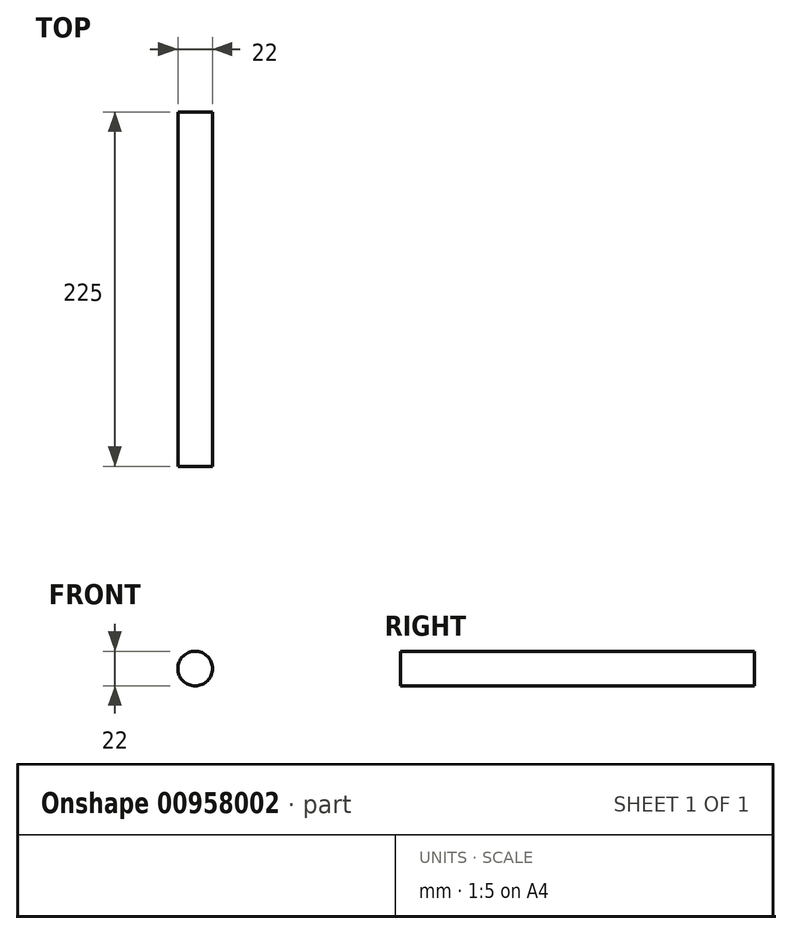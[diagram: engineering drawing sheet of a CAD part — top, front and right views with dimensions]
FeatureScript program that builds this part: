
annotation { "Feature Type Name" : "Feature", "Feature Type Description" : "" }
export const myFeature = defineFeature(function(context is Context, id is Id, definition is map)
    precondition{}
    {
        {
            var Q0;
            Q0=qCreatedBy(makeId("Front.planeOp"),FACE);
            var sketch = newSketch(context, id + "F0", { "sketchPlane" : qUnion([Q0])});
            skCircle(sketch, "E0", {"center": v(0, 0) * mm, "radius": 11 * mm});
            skSolve(sketch);
        }
        {
            var Q0;
            Q0 = qSketchRegion(id + "F0", true);
            extrude(context, id + "F1", {"entities" : qUnion([Q0]), "endBound" : BoundingType.SYMMETRIC, "depth" : 225 * mm, "offsetDistance" : 25 * mm});
        }
    });
